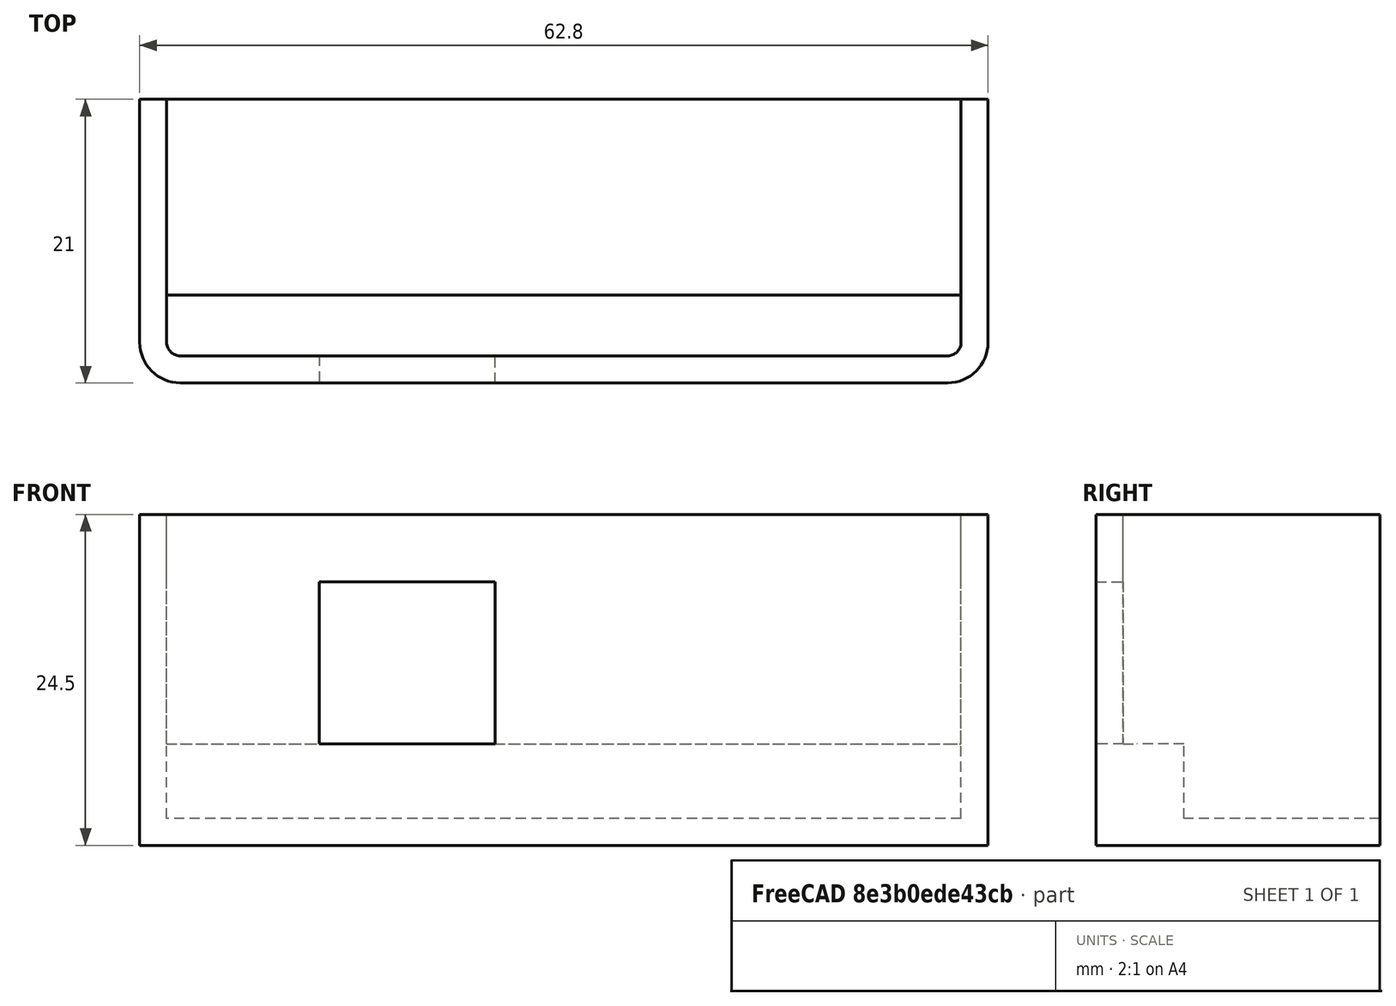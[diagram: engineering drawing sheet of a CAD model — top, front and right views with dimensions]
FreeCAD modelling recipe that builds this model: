
FCSTD DOCUMENT  (FreeCAD 0.20R28671 (Git))
Label: carcasa arduino
License: All rights reserved
LicenseURL: http://en.wikipedia.org/wiki/All_rights_reserved
objects: TechDraw::DrawViewDimension×14, PartDesign::Pad×7, Sketcher::SketchObject×5, TechDraw::DrawViewAnnotation×3, TechDraw::DrawProjGroupItem×2, PartDesign::Fillet×1, PartDesign::Pocket×1, PartDesign::Body×1, TechDraw::DrawSVGTemplate×1, Part::Refine×1, TechDraw::DrawProjGroup×1, TechDraw::DrawViewSection×1, TechDraw::DrawViewSymbol×1, TechDraw::DrawPage×1
note: 25 computed .brp shape members not serialized (recipe doc carries the construction recipe); baked Part::Feature solids carry a one-line shape summary decoded from their .brp

FEATURE [Sketcher::SketchObject] Sketch
  FullyConstrained = true
  MapMode = 5
  Support = -> [XY_Plane]
  sketch-geometry (6):
    g0: LineSegment StartX=-31.4 StartY=0 StartZ=0 EndX=31.4 EndY=0 EndZ=0
    g1: LineSegment StartX=31.4 StartY=0 StartZ=0 EndX=31.4 EndY=21 EndZ=0
    g2: LineSegment StartX=31.4 StartY=21 StartZ=0 EndX=-31.4 EndY=21 EndZ=0
    g3: LineSegment StartX=-31.4 StartY=21 StartZ=0 EndX=-31.4 EndY=0 EndZ=0
    g4: LineSegment StartX=-31.4 StartY=0 StartZ=0 EndX=0 EndY=0 EndZ=0
    g5: LineSegment StartX=0 StartY=0 StartZ=0 EndX=31.4 EndY=0 EndZ=0
  constraints (16):
    c: Coincident(g0,g1)
    c: Coincident(g1,g2)
    c: Coincident(g2,g3)
    c: Coincident(g3,g0)
    c: Horizontal(g0)
    c: Horizontal(g2)
    c: Vertical(g1)
    c: Vertical(g3)
    c: PointOnObject(g0,g-1)
    c: Coincident(g4,g0)
    c: Coincident(g5,g4)
    c: Coincident(g5,g0)
    c: Equal(g5,g4)
    c: Coincident(g4,g-1)
    c: DistanceX(g0,g0) = 62.8
    c: DistanceY(g3,g3) = 21
FEATURE [PartDesign::Pad] Pad
  Direction = (0,0,1)
  Length = 2
  Length2 = 100
  Profile = -> Sketch
  ReferenceAxis = -> Sketch [N_Axis]
  Type = 0
FEATURE [PartDesign::Fillet] Fillet
  Base = -> Pad [Edge1,Edge2]
  BaseFeature = -> Pad
  Radius = 3
  SupportTransform = false
  UseAllEdges = false
FEATURE [Sketcher::SketchObject] Sketch001
  ExternalGeometry = -> [Fillet]
  FullyConstrained = true
  MapMode = 5
  Placement = pos=(0,0,2) rot=(0,0,1;0rad)
  Support = -> [Fillet]
  sketch-geometry (6):
    g0: LineSegment StartX=-28.4 StartY=-4e-16 StartZ=0 EndX=28.4 EndY=-4e-16 EndZ=0
    g1: ArcOfCircle CenterX=28.4 CenterY=3 CenterZ=0 NormalX=0 NormalY=0 NormalZ=1 AngleXU=0 Radius=3 StartAngle=4.71239 EndAngle=6.28319
    g2: ArcOfCircle CenterX=-28.4 CenterY=3 CenterZ=0 NormalX=0 NormalY=0 NormalZ=1 AngleXU=0 Radius=3 StartAngle=3.14159 EndAngle=4.71239
    g3: LineSegment StartX=-31.4 StartY=3 StartZ=0 EndX=-31.4 EndY=6.5 EndZ=0
    g4: LineSegment StartX=-31.4 StartY=6.5 StartZ=0 EndX=31.4 EndY=6.5 EndZ=0
    g5: LineSegment StartX=31.4 StartY=6.5 StartZ=0 EndX=31.4 EndY=3 EndZ=0
  constraints (15):
    c: Coincident(g0,g-6)
    c: Coincident(g0,g-5)
    c: Coincident(g1,g-5)
    c: Coincident(g2,g-6)
    c: Coincident(g2,g0)
    c: Tangent(g2,g-6)
    c: Tangent(g1,g0) = -1.5708
    c: Coincident(g3,g2)
    c: Vertical(g3)
    c: Coincident(g4,g3)
    c: PointOnObject(g4,g-4)
    c: Horizontal(g4)
    c: Coincident(g5,g4)
    c: Coincident(g5,g1)
    c: DistanceY(g-1,g3) = 6.5
FEATURE [PartDesign::Pad] Pad001
  BaseFeature = -> Fillet
  Direction = (0,0,1)
  Length = 5.5
  Length2 = 100
  Profile = -> Sketch001
  ReferenceAxis = -> Sketch001 [N_Axis]
  Type = 0
FEATURE [Sketcher::SketchObject] Sketch002
  ExternalGeometry = -> [Pad001]
  FullyConstrained = true
  MapMode = 5
  Placement = pos=(0,0,2) rot=(0,0,1;0rad)
  Support = -> [Pad001]
  sketch-geometry (8):
    g0: LineSegment StartX=-31.4 StartY=21 StartZ=0 EndX=-29.4 EndY=21 EndZ=0
    g1: LineSegment StartX=-29.4 StartY=21 StartZ=0 EndX=-29.4 EndY=6.5 EndZ=0
    g2: LineSegment StartX=-29.4 StartY=6.5 StartZ=0 EndX=-31.4 EndY=6.5 EndZ=0
    g3: LineSegment StartX=-31.4 StartY=6.5 StartZ=0 EndX=-31.4 EndY=21 EndZ=0
    g4: LineSegment StartX=31.4 StartY=21 StartZ=0 EndX=29.4 EndY=21 EndZ=0
    g5: LineSegment StartX=29.4 StartY=21 StartZ=0 EndX=29.4 EndY=6.5 EndZ=0
    g6: LineSegment StartX=29.4 StartY=6.5 StartZ=0 EndX=31.4 EndY=6.5 EndZ=0
    g7: LineSegment StartX=31.4 StartY=6.5 StartZ=0 EndX=31.4 EndY=21 EndZ=0
  constraints (21):
    c: Coincident(g0,g1)
    c: Coincident(g1,g2)
    c: Coincident(g2,g3)
    c: Coincident(g3,g0)
    c: Horizontal(g0)
    c: Horizontal(g2)
    c: Vertical(g1)
    c: Coincident(g0,g-3)
    c: Coincident(g4,g5)
    c: Coincident(g5,g6)
    c: Coincident(g6,g7)
    c: Coincident(g7,g4)
    c: Horizontal(g4)
    c: Horizontal(g6)
    c: Vertical(g5)
    c: Vertical(g7)
    c: Coincident(g4,g-4)
    c: Coincident(g2,g-3)
    c: Equal(g5,g1)
    c: Equal(g0,g4)
    c: DistanceX(g0,g0) = 2
FEATURE [PartDesign::Pad] Pad002
  BaseFeature = -> Pad001
  Direction = (0,0,1)
  Length = 10
  Length2 = 100
  Profile = -> Sketch002
  ReferenceAxis = -> Sketch002 [N_Axis]
  Type = 3
  UpToFace = -> Pad001 [Face11]
FEATURE [Sketcher::SketchObject] Sketch003
  ExternalGeometry = -> [Pad002]
  FullyConstrained = true
  MapMode = 5
  Placement = pos=(0,0,7.5) rot=(0,0,1;0rad)
  Support = -> [Pad002]
  sketch-geometry (13):
    g0: LineSegment StartX=-28.4 StartY=-4e-16 StartZ=0 EndX=28.4 EndY=4.3507e-12 EndZ=0
    g1: LineSegment StartX=31.4 StartY=3 StartZ=0 EndX=31.4 EndY=21 EndZ=0
    g2: ArcOfCircle CenterX=-28.4 CenterY=3 CenterZ=0 NormalX=0 NormalY=0 NormalZ=1 AngleXU=0 Radius=3 StartAngle=3.14159 EndAngle=4.71239
    g3: LineSegment StartX=-31.4 StartY=21 StartZ=0 EndX=-31.4 EndY=3 EndZ=0
    g4: LineSegment StartX=-31.4 StartY=21 StartZ=0 EndX=-29.4 EndY=21 EndZ=0
    g5: LineSegment StartX=29.4 StartY=21 StartZ=0 EndX=31.4 EndY=21 EndZ=0
    g6: ArcOfCircle CenterX=28.4 CenterY=3 CenterZ=0 NormalX=0 NormalY=0 NormalZ=1 AngleXU=0 Radius=3 StartAngle=4.71239 EndAngle=6.28319
    g7: LineSegment StartX=-29.4 StartY=21 StartZ=0 EndX=-29.4 EndY=3 EndZ=0
    g8: LineSegment StartX=29.4 StartY=21 StartZ=0 EndX=29.4 EndY=3 EndZ=0
    g9: LineSegment StartX=-28.4 StartY=2 StartZ=0 EndX=28.4 EndY=2 EndZ=0
    g10: ArcOfCircle CenterX=-28.4 CenterY=3 CenterZ=0 NormalX=0 NormalY=0 NormalZ=1 AngleXU=0 Radius=1 StartAngle=3.14159 EndAngle=4.71239
    g11: ArcOfCircle CenterX=28.4 CenterY=3 CenterZ=0 NormalX=0 NormalY=0 NormalZ=1 AngleXU=0 Radius=1 StartAngle=4.71239 EndAngle=6.28319
    g12: LineSegment StartX=0 StartY=0 StartZ=0 EndX=0 EndY=2 EndZ=0
  constraints (30):
    c: Coincident(g0,g-4)
    c: Coincident(g0,g-5)
    c: Coincident(g1,g-5)
    c: Coincident(g1,g-6)
    c: Coincident(g2,g-4)
    c: Coincident(g2,g0)
    c: Tangent(g2,g-4)
    c: Coincident(g3,g-3)
    c: Coincident(g3,g2)
    c: Coincident(g4,g3)
    c: Coincident(g4,g-7)
    c: Coincident(g5,g-8)
    c: Coincident(g5,g1)
    c: Coincident(g6,g1)
    c: Coincident(g6,g0)
    c: Tangent(g6,g-5)
    c: Coincident(g7,g4)
    c: Vertical(g7)
    c: Coincident(g8,g5)
    c: Vertical(g8)
    c: Horizontal(g9)
    c: Tangent(g10,g7) = -1.5708
    c: Tangent(g10,g9) = -1.5708
    c: Tangent(g11,g9) = -1.5708
    c: Tangent(g11,g8) = 1.5708
    c: Equal(g11,g10)
    c: Coincident(g12,g-1)
    c: PointOnObject(g12,g9)
    c: Vertical(g12)
    c: Coincident(g2,g10)
FEATURE [PartDesign::Pad] Pad003
  BaseFeature = -> Pad002
  Direction = (0,0,1)
  Length = 12
  Length2 = 100
  Profile = -> Sketch003
  ReferenceAxis = -> Sketch003 [N_Axis]
  Type = 0
FEATURE [Sketcher::SketchObject] Sketch004
  ExternalGeometry = -> [Pad003]
  FullyConstrained = true
  MapMode = 5
  Placement = pos=(0,0,19.5) rot=(0,0,1;0rad)
  Support = -> [Pad003]
  sketch-geometry (8):
    g0: LineSegment StartX=-26.6 StartY=0 StartZ=0 EndX=0 EndY=0 EndZ=0
    g1: LineSegment StartX=0 StartY=0 StartZ=0 EndX=26.6 EndY=0 EndZ=0
    g2: LineSegment StartX=-18.1 StartY=0 StartZ=0 EndX=-5.1 EndY=0 EndZ=0
    g3: LineSegment StartX=-5.1 StartY=0 StartZ=0 EndX=-5.1 EndY=2 EndZ=0
    g4: LineSegment StartX=-5.1 StartY=2 StartZ=0 EndX=-18.1 EndY=2 EndZ=0
    g5: LineSegment StartX=-18.1 StartY=2 StartZ=0 EndX=-18.1 EndY=0 EndZ=0
    g6: LineSegment StartX=-18.1 StartY=0 StartZ=0 EndX=-11.6 EndY=1 EndZ=0
    g7: LineSegment StartX=-11.6 StartY=1 StartZ=0 EndX=-5.1 EndY=2 EndZ=0
  constraints (23):
    c: Coincident(g0,g-1)
    c: Coincident(g1,g-1)
    c: Equal(g1,g0)
    c: Horizontal(g0)
    c: Horizontal(g1)
    c: DistanceX(g0,g1) = 53.2
    c: Coincident(g2,g3)
    c: Coincident(g3,g4)
    c: Coincident(g4,g5)
    c: Coincident(g5,g2)
    c: Horizontal(g2)
    c: Horizontal(g4)
    c: Vertical(g3)
    c: Vertical(g5)
    c: PointOnObject(g2,g0)
    c: Horizontal(g-3,g4)
    c: Coincident(g6,g2)
    c: Coincident(g7,g6)
    c: Coincident(g7,g3)
    c: Equal(g7,g6)
    c: Parallel(g6,g7)
    c: DistanceX(g0,g6) = 15
    c: DistanceX(g2,g2) = 13
FEATURE [PartDesign::Pocket] Pocket
  BaseFeature = -> Pad003
  Direction = (0,0,-1)
  Length = 0
  Length2 = 100
  Profile = -> Sketch004
  Type = 3
  UpToFace = -> Pad003 [Face34]
FEATURE [PartDesign::Pad] Pad004
  BaseFeature = -> Pocket
  Direction = (0,0,1)
  Length = 5
  Length2 = 100
  Profile = -> Pocket [Face24]
  Type = 0
FEATURE [PartDesign::Pad] Pad005
  BaseFeature = -> Pad004
  Direction = (0,0,1)
  Length = 5
  Length2 = 100
  Profile = -> Pad004 [Face27]
  Type = 0
FEATURE [PartDesign::Pad] Pad006
  BaseFeature = -> Pad005
  Direction = (-1,0,0)
  Length = 13
  Length2 = 100
  Profile = -> Pad005 [Face45]
  Type = 0
FEATURE [PartDesign::Body] Body
  Group = -> [Sketch,Pad,Fillet,Sketch001,Pad001,Sketch002,Pad002,Sketch003,Pad003,Sketch004,Pocket,Pad004,Pad005,Pad006]
  Origin = -> Origin
  Tip = -> Pad006
FEATURE [TechDraw::DrawSVGTemplate] Template003
  EditableTexts = AUTHOR_NAME=Daniel García García; DATE=13-04-2022; DN=6; DOCUMENT_TYPE=Plano de pieza; PN=7; REVISION=1; SCALE=1:1; SHEET=6/15; SIZE=A4; TITLELINE-1=Carcasa para Arduino
  Height = 210
  Orientation = 1
  Width = 297
FEATURE [Part::Refine] Pad006001
  Source = -> Pad006
FEATURE [TechDraw::DrawProjGroupItem] ProjItem  label="Front"
  CoarseView = false
  Direction = (0,-1,0)
  Focus = 100
  HardHidden = false
  IsoCount = 0
  IsoHidden = false
  IsoVisible = false
  LockPosition = true
  Perspective = false
  Rotation = 0
  RotationVector = (1,0,0)
  ScaleType = 2
  SeamHidden = false
  SeamVisible = true
  SmoothHidden = false
  SmoothVisible = true
  Source = -> [Pad006001]
  Type = 0
  X = 0
  XDirection = (1,0,0)
  Y = 0
FEATURE [TechDraw::DrawProjGroupItem] ProjItem001  label="Top"
  CoarseView = false
  Direction = (0,0,1)
  Focus = 100
  HardHidden = false
  IsoCount = 0
  IsoHidden = false
  IsoVisible = false
  LockPosition = true
  Perspective = false
  Rotation = 0
  RotationVector = (1,0,0)
  ScaleType = 2
  SeamHidden = false
  SeamVisible = true
  SmoothHidden = false
  SmoothVisible = true
  Source = -> [Pad006001]
  Type = 4
  X = 0
  XDirection = (1,0,0)
  Y = -62.8571
FEATURE [TechDraw::DrawProjGroup] ProjGroup
  Anchor = -> ProjItem
  AutoDistribute = true
  LockPosition = false
  ProjectionType = 0
  Rotation = 0
  ScaleType = 0
  Source = -> [Pad006001]
  Views = -> [ProjItem,ProjItem001]
  X = 200
  Y = 152.5
  spacingX = 15
  spacingY = 15
FEATURE [TechDraw::DrawViewSection] SectionView  label="Section A - A"
  BaseView = -> ProjItem
  CoarseView = false
  CutSurfaceDisplay = 2
  Direction = (1,0,0)
  FileGeomPattern = <path>
  FileHatchPattern = <path>
  Focus = 100
  FuseBeforeCut = false
  HardHidden = false
  HatchScale = 1
  IsoCount = 0
  IsoHidden = false
  IsoVisible = false
  LockPosition = true
  NameGeomPattern = Diamond
  Perspective = false
  Rotation = 0
  ScaleType = 2
  SeamHidden = false
  SeamVisible = true
  SectionDirection = 1
  SectionNormal = (1,0,0)
  SectionOrigin = (-11,10.5,12.25)
  SectionSymbol = A
  SmoothHidden = false
  SmoothVisible = true
  Source = -> [Pad006001]
  X = 75.1071
  XDirection = (0,1,0)
  Y = 152.5
FEATURE [TechDraw::DrawViewDimension] Dimension
  AngleOverride = false
  Arbitrary = false
  ArbitraryTolerances = false
  EqualTolerance = true
  ExtensionAngle = 0
  FormatSpec = R%.2w
  FormatSpecOverTolerance = %+.2w
  FormatSpecUnderTolerance = %+.2w
  Inverted = false
  LineAngle = 0
  LockPosition = false
  MeasureType = 1
  OverTolerance = 0
  References2D = -> [ProjItem001]
  Rotation = 0
  ScaleType = 0
  TheoreticalExact = false
  Type = 4
  UnderTolerance = 0
  X = -42.8443
  Y = -10.0232
FEATURE [TechDraw::DrawViewDimension] Dimension001
  AngleOverride = false
  Arbitrary = false
  ArbitraryTolerances = false
  EqualTolerance = true
  ExtensionAngle = 0
  FormatSpec = %.2w
  FormatSpecOverTolerance = %+.2w
  FormatSpecUnderTolerance = %+.2w
  Inverted = false
  LineAngle = 0
  LockPosition = false
  MeasureType = 1
  OverTolerance = 0
  References2D = -> [ProjItem001]
  Rotation = 0
  ScaleType = 0
  TheoreticalExact = false
  Type = 2
  UnderTolerance = 0
  X = 43.3166
  Y = 3.47991
FEATURE [TechDraw::DrawViewDimension] Dimension002
  AngleOverride = false
  Arbitrary = false
  ArbitraryTolerances = false
  EqualTolerance = true
  ExtensionAngle = 0
  FormatSpec = %.2w
  FormatSpecOverTolerance = %+.2w
  FormatSpecUnderTolerance = %+.2w
  Inverted = false
  LineAngle = 0
  LockPosition = false
  MeasureType = 1
  OverTolerance = 0
  References2D = -> [SectionView]
  Rotation = 0
  ScaleType = 0
  TheoreticalExact = false
  Type = 2
  UnderTolerance = 0
  X = 27.2816
  Y = -5.65511
FEATURE [TechDraw::DrawViewDimension] Dimension003
  AngleOverride = false
  Arbitrary = false
  ArbitraryTolerances = false
  EqualTolerance = true
  ExtensionAngle = 0
  FormatSpec = %.2w
  FormatSpecOverTolerance = %+.2w
  FormatSpecUnderTolerance = %+.2w
  Inverted = false
  LineAngle = 0
  LockPosition = false
  MeasureType = 1
  OverTolerance = 0
  References2D = -> [SectionView]
  Rotation = 0
  ScaleType = 0
  TheoreticalExact = false
  Type = 1
  UnderTolerance = 0
  X = -6.57756
  Y = 22.4805
FEATURE [TechDraw::DrawViewDimension] Dimension004
  AngleOverride = false
  Arbitrary = false
  ArbitraryTolerances = false
  EqualTolerance = true
  ExtensionAngle = 0
  FormatSpec = %.2w
  FormatSpecOverTolerance = %+.2w
  FormatSpecUnderTolerance = %+.2w
  Inverted = false
  LineAngle = 0
  LockPosition = false
  MeasureType = 1
  OverTolerance = 0
  References2D = -> [ProjItem]
  Rotation = 0
  ScaleType = 0
  TheoreticalExact = false
  Type = 2
  UnderTolerance = 0
  X = 2.91856
  Y = 3.75
FEATURE [TechDraw::DrawViewDimension] Dimension005
  AngleOverride = false
  Arbitrary = false
  ArbitraryTolerances = false
  EqualTolerance = true
  ExtensionAngle = 0
  FormatSpec = %.2w
  FormatSpecOverTolerance = %+.2w
  FormatSpecUnderTolerance = %+.2w
  Inverted = false
  LineAngle = 0
  LockPosition = false
  MeasureType = 1
  OverTolerance = 0
  References2D = -> [ProjItem]
  Rotation = 0
  ScaleType = 0
  TheoreticalExact = false
  Type = 1
  UnderTolerance = 0
  X = -21.0336
  Y = -5.06678
FEATURE [TechDraw::DrawViewDimension] Dimension006
  AngleOverride = false
  Arbitrary = false
  ArbitraryTolerances = false
  EqualTolerance = true
  ExtensionAngle = 0
  FormatSpec = %.2w
  FormatSpecOverTolerance = %+.2w
  FormatSpecUnderTolerance = %+.2w
  Inverted = false
  LineAngle = 0
  LockPosition = false
  MeasureType = 1
  OverTolerance = 0
  References2D = -> [ProjItem]
  Rotation = 0
  ScaleType = 0
  TheoreticalExact = false
  Type = 2
  UnderTolerance = 0
  X = 39.3242
  Y = 1.93398
FEATURE [TechDraw::DrawViewDimension] Dimension007
  AngleOverride = false
  Arbitrary = false
  ArbitraryTolerances = false
  EqualTolerance = true
  ExtensionAngle = 0
  FormatSpec = %.2w
  FormatSpecOverTolerance = %+.2w
  FormatSpecUnderTolerance = %+.2w
  Inverted = false
  LineAngle = 0
  LockPosition = false
  MeasureType = 1
  OverTolerance = 0
  References2D = -> [ProjItem001]
  Rotation = 0
  ScaleType = 0
  TheoreticalExact = false
  Type = 1
  UnderTolerance = 0
  X = -0.849024
  Y = 26.2542
FEATURE [TechDraw::DrawViewDimension] Dimension008
  AngleOverride = false
  Arbitrary = false
  ArbitraryTolerances = false
  EqualTolerance = true
  ExtensionAngle = 0
  FormatSpec = %.2w
  FormatSpecOverTolerance = %+.2w
  FormatSpecUnderTolerance = %+.2w
  Inverted = false
  LineAngle = 0
  LockPosition = false
  MeasureType = 1
  OverTolerance = 0
  References2D = -> [ProjItem001]
  Rotation = 0
  ScaleType = 0
  TheoreticalExact = false
  Type = 1
  UnderTolerance = 0
  X = -23.089
  Y = 18.896
FEATURE [TechDraw::DrawViewDimension] Dimension009
  AngleOverride = false
  Arbitrary = false
  ArbitraryTolerances = false
  EqualTolerance = true
  ExtensionAngle = 0
  FormatSpec = %.2w
  FormatSpecOverTolerance = %+.2w
  FormatSpecUnderTolerance = %+.2w
  Inverted = false
  LineAngle = 0
  LockPosition = false
  MeasureType = 1
  OverTolerance = 0
  References2D = -> [ProjItem001]
  Rotation = 0
  ScaleType = 0
  TheoreticalExact = false
  Type = 2
  UnderTolerance = 0
  X = 21.3248
  Y = -11.481
FEATURE [TechDraw::DrawViewDimension] Dimension010
  AngleOverride = false
  Arbitrary = false
  ArbitraryTolerances = false
  EqualTolerance = true
  ExtensionAngle = 0
  FormatSpec = %.2w
  FormatSpecOverTolerance = %+.2w
  FormatSpecUnderTolerance = %+.2w
  Inverted = false
  LineAngle = 0
  LockPosition = false
  MeasureType = 1
  OverTolerance = 0
  References2D = -> [SectionView]
  Rotation = 0
  ScaleType = 0
  TheoreticalExact = false
  Type = 1
  UnderTolerance = 0
  X = -18.4705
  Y = 12.4411
FEATURE [TechDraw::DrawViewDimension] Dimension011
  AngleOverride = false
  Arbitrary = false
  ArbitraryTolerances = false
  EqualTolerance = true
  ExtensionAngle = 0
  FormatSpec = %.2w
  FormatSpecOverTolerance = %+.2w
  FormatSpecUnderTolerance = %+.2w
  Inverted = false
  LineAngle = 0
  LockPosition = false
  MeasureType = 1
  OverTolerance = 0
  References2D = -> [SectionView]
  Rotation = 0
  ScaleType = 0
  TheoreticalExact = false
  Type = 2
  UnderTolerance = 0
  X = 15.9593
  Y = -12.5715
FEATURE [TechDraw::DrawViewAnnotation] Annotation
  Font = osifont
  LineSpace = 80
  LockPosition = false
  MaxWidth = -1
  Rotation = 0
  ScaleType = 0
  Text = Sección A-A'
  TextSize = 5
  TextStyle = 0
  X = 78.88
  Y = 124.811
FEATURE [TechDraw::DrawViewDimension] Dimension012
  AngleOverride = false
  Arbitrary = false
  ArbitraryTolerances = false
  EqualTolerance = true
  ExtensionAngle = 0
  FormatSpec = %.2w
  FormatSpecOverTolerance = %+.2w
  FormatSpecUnderTolerance = %+.2w
  Inverted = false
  LineAngle = 0
  LockPosition = false
  MeasureType = 1
  OverTolerance = 0
  References2D = -> [ProjItem]
  Rotation = 0
  ScaleType = 0
  TheoreticalExact = false
  Type = 2
  UnderTolerance = 0
  X = -40.7022
  Y = -6.23584
FEATURE [TechDraw::DrawViewDimension] Dimension014
  AngleOverride = false
  Arbitrary = false
  ArbitraryTolerances = false
  EqualTolerance = true
  ExtensionAngle = 0
  FormatSpec = %.2w
  FormatSpecOverTolerance = %+.2w
  FormatSpecUnderTolerance = %+.2w
  Inverted = false
  LineAngle = 0
  LockPosition = false
  MeasureType = 1
  OverTolerance = 0
  References2D = -> [ProjItem]
  Rotation = 0
  ScaleType = 0
  TheoreticalExact = false
  Type = 1
  UnderTolerance = 0
  X = 13.15
  Y = 21.9194
FEATURE [TechDraw::DrawViewSymbol] Symbol
  LockPosition = false
  Rotation = 0
  Scale = 0.3
  ScaleType = 2
  Symbol = <blob: 2444 chars omitted>
  X = 217.487
  Y = 36.9001
FEATURE [TechDraw::DrawViewAnnotation] Annotation001
  Font = osifont
  LineSpace = 80
  LockPosition = false
  MaxWidth = -1
  Rotation = 0
  ScaleType = 0
  Text = Default Text
  TextSize = 5
  TextStyle = 0
  X = 148.5
  Y = 105
FEATURE [TechDraw::DrawViewAnnotation] Annotation002
  Font = osifont
  LineSpace = 80
  LockPosition = false
  MaxWidth = -1
  Rotation = 0
  ScaleType = 0
  Text = '
  TextSize = 5
  TextStyle = 0
  X = 190.973
  Y = 123.12
FEATURE [TechDraw::DrawPage] Page003  label="Carcasa para Arduino"
  KeepUpdated = true
  NextBalloonIndex = 1
  ProjectionType = 0
  Template = -> Template003
  Views = -> [ProjGroup,SectionView,Dimension,Dimension001,Dimension002,Dimension003,Dimension004,Dimension005,Dimension006,Dimension007,Dimension008,Dimension009,Dimension010,Dimension011,Annotation,Dimension012,Dimension014,Symbol,Annotation002]
note: 2 file-system paths scrubbed to <path> (originals preserved in the JSON sidecar)
